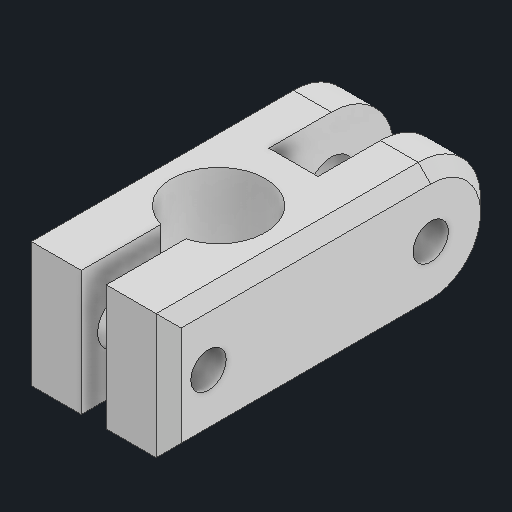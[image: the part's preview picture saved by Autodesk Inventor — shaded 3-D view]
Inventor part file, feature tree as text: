
AUTODESK INVENTOR PART (.ipt)
format: ipt  version: 2025.1 (Build 291241020, 241B)  size: 170,496 bytes
history: native  units: in
note: dims shown in document units (in); Inventor stores cm internally (conversion verified against a paired STEP export)
features: sketch x3, extrude x2, hole x2, projected_geometry x2, fillet x1, chamfer x1
ambient origin geometry x8: Origin, YZ Plane, XZ Plane, XY Plane, X Axis, Y Axis, Z Axis, Center Point
bodies: Solid1 (feature_tree)
feature tree (11):
  extrude  "Extrusion1"  Depth=0.3in
  sketch  "Sketch2"  dims[d2=0.3in d3=0.8in d4=0.5in]
  hole  "Hole1"  [1 undecoded]
  fillet  "Fillet1"  Radius=0.5in
  extrude  "Extrusion2"  Depth=0.25in
  chamfer  "Chamfer1"  Distance=0.5in
  hole  "Hole2"  [1 undecoded]
  sketch  "Sketch1"  dims[d0=0.375in d1=0.3in]
  projected_geometry  "Projected Loop1"
  sketch  "Sketch3"  dims[d6=0.05in d7=0.05in d8=0.5in d9=0.0in d10=0.1378in d11=0.1595in d12=0.142in d13=0.236in d14=0.248in d15=0.25in d16=90.0deg d17=0.197in d18=0.8108in d19=0.25in d20=0.1181in d21=0.25in d22=0.0984in d23=0.0984in d24=0.0in d25=0.0in d26=0.5in d27=0.05in d28=0.125in d29=45.0deg d30=0.189in d31=0.75in d32=0.37in d33=0.25in d34=90.0deg d35=1.0in d36=0.8108in]
  projected_geometry  "Projected Loop2"
note: 2 required parameter values undecoded (feature->parameter linkage not recoverable at this tier; creation-order binding heuristic only, values carry confidence <= 0.55)
